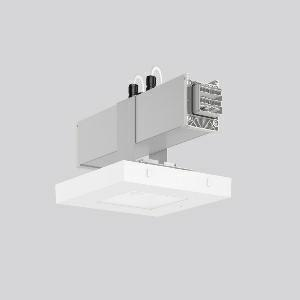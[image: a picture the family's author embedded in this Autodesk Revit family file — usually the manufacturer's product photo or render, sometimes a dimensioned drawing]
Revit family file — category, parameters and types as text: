
# Revit family: linedo_module_rw_9503rw_760_437_000_73c8
name_source: partatom
category: Lighting Fixtures
units: mm (PartAtom-declared; Revit-internal decimal feet)

## family parameters
Cut with Voids When Loaded = No
Host = Face
Light Source = No
Part Type = Normal
Room Calculation Point = No
Round Connector Dimension = Use Diameter
Shared = No

## types (1)
- LINEDO Module RW (1 x LED Modul 765, 390 lm, 6500)
    Apparent Load = 7 VA
    CIE Flux Codes = 37 69 99 100 100
    Color Rendering = 70
    Color Temperature = 6500
    Default Elevation = 1800 mm
    Description = LINEDO, 6,7 W, 390 lm, 765, silver, on/off
Continuous line luminaire, L 330 B 198 H 170, SBS, 3 h, emergency-310 lm, DALI-Sibe
    Height = 170 mm  [stored 0.557743 ft]
    Lamp = 1 x LED Modul 765
    Lamp Light Flux = 390 lm
    Lamp count = 1
    Length = 330 mm
    Lifetime = 50000 h
    Luminous efficacy = 58 lm/W
    Manufacturer = RZB
    ModVariant = No
    Model = 9503RW.760.437.000
    Mounting Place = Ceiling
    Mounting Type = Surface mounted, Pendant
    Number of Poles = 1
    OnlyDefault = Yes
    Power Factor = 1
    Product Name = LINEDO Module RW
    Product group = Surface mounted continuous line luminaire system
    ProductGroupID = 310
    Protection Class = Protection class I
    Protection Degree = IP 54
    RLX_Detail_Level = 1
    RLX_Emergency_Light_Flux = 310 lm
    RLX_Emergency_Type = 3
    RLX_Emergency_Type_DB = Yes
    RlxData = <blob elided: 40665 chars, md5=e4d6988a>
    Socket = socket
    Standby Power = 0 W
    System Light Flux = 390 lm
    System Power = 7 W
    Type Comments = Product without accessories
    Type Image = 9503rw.760.434.000.jpg
    URL = http://relux.com
    VarID = ---
    Voltage = 230 V
    Voltage Range = 220-240 V
    Weight = 0.00 kg
    Width = 198 mm

note: [stored X ft] marks values corroborated as IEEE doubles in the binary element streams (Revit-internal decimal feet)

## geometry (parser evidence)
native form markers: Blend x4, Sweep x14
no freeform markers — native parametric forms only
